# Revit family: CA4060001_Mezclador Ducha Cascade 8 pulgadas palanca
name_source: partatom
category: Plumbing Fixtures
units: mm (PartAtom-declared; Revit-internal decimal feet)

## family parameters
Always vertical = Yes
Cut with Voids When Loaded = No
OmniClass Number = 23.21.21.19
OmniClass Title = Commercial Dishwasher Equipment
Part Type = Normal
Room Calculation Point = No
Round Connector Dimension = Use Diameter
Shared = No
Work Plane-Based = No

## types (1)
- CA4060001_Mezclador Ducha Cascade 8 pulgadas palanca
    Acabado = Cromado
    Alto = 6 cm
    Ancho = 6.5 cm
    Colección = Cascade
    Description = La línea de griferías y accesorios Cascade se inspira en la fluidez natural del agua. Además, cuenta con tecnología DuraCrome ¡Lee más sobre sus características!
    Garantía = 30 años en estructura
    Garantías de otros componentes = 5 años en acabados
    Incluye = Cuerpo mezclador, manijas
    Largo = 13.8 cm
    Línea = Cascade
    Material = Corona_Cromado
    Materiales = Polímero de alta ingeniería, Metal
    Resistencia = Resistente a la corrosión pelado y decoloración por agua
    Tecnologías = DuraCrome
    URL = https://corona.co
    Uso = Residencial

## geometry (parser evidence)
native form markers: Sweep x4
no freeform markers — native parametric forms only
